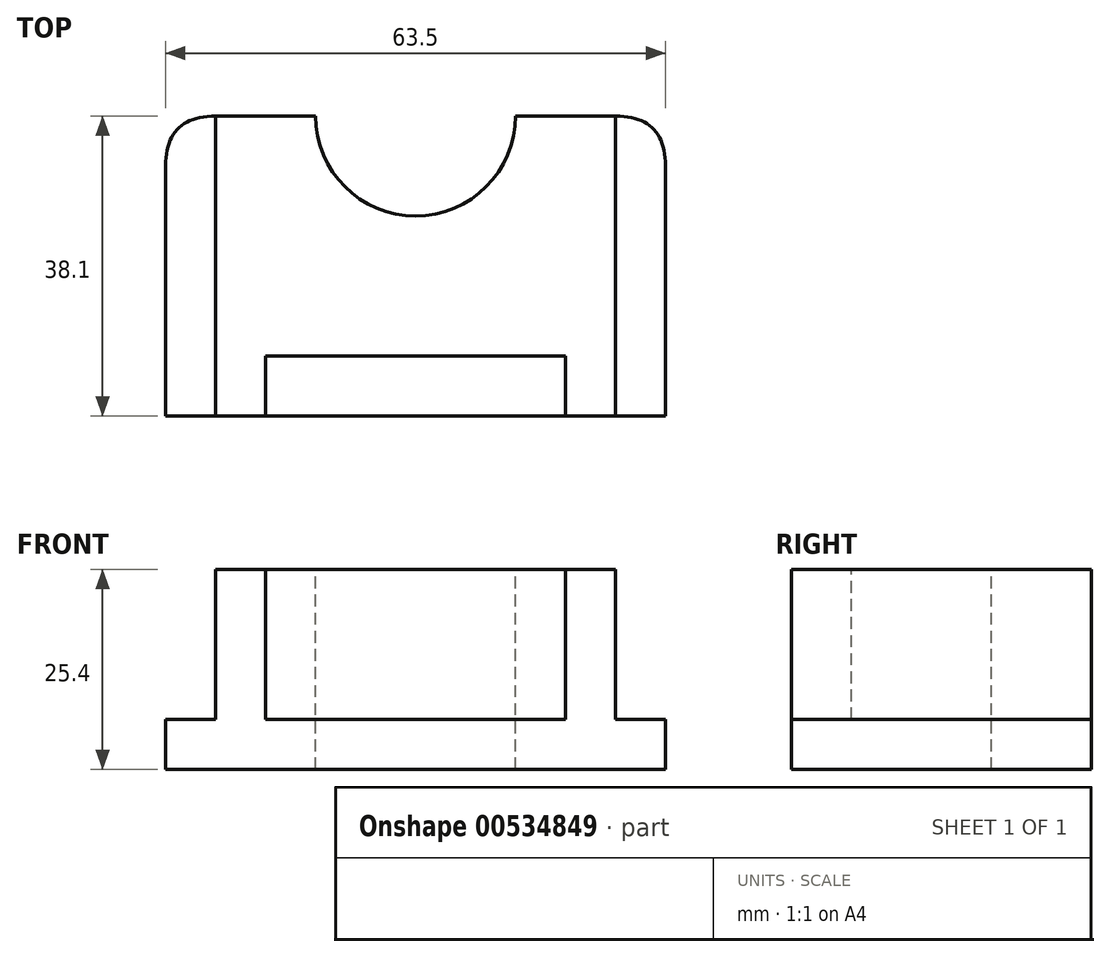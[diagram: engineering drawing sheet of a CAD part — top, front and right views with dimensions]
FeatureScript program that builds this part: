
annotation { "Feature Type Name" : "Feature", "Feature Type Description" : "" }
export const myFeature = defineFeature(function(context is Context, id is Id, definition is map)
    precondition{}
    {
        {
            var Q0;
            Q0=qCreatedBy(makeId("Top.planeOp"),FACE);
            var sketch = newSketch(context, id + "F0", { "sketchPlane" : qUnion([Q0])});
            skLineSegment(sketch, "E0.bottom", {"start": v(31.75, -19.05) * mm, "end": v(-31.75, -19.05) * mm});
            skLineSegment(sketch, "E0.top", {"start": v(31.75, 19.05) * mm, "end": v(-31.75, 19.05) * mm});
            skLineSegment(sketch, "E0.left", {"start": v(31.75, -19.05) * mm, "end": v(31.75, 19.05) * mm});
            skLineSegment(sketch, "E0.right", {"start": v(-31.75, -19.05) * mm, "end": v(-31.75, 19.05) * mm});
            skPoint(sketch, "E0.middle", {"position": v(0, 0) * mm});
            skSolve(sketch);
        }
        {
            var Q0;
            Q0 = qSketchRegion(id + "F0", true);
            extrude(context, id + "F1", {"entities" : qUnion([Q0]), "depth" : 6.35 * mm, "offsetDistance" : 25.4 * mm});
        }
        {
            var Q0;
            Q0=makeQuery(id+"F1.opExtrude","SWEPT_EDGE",EDGE,{"disambiguationData":[OSD([sQuery(id+"F0.wireOp",EDGE,"E0.top"),sQuery(id+"F0.wireOp",EDGE,"E0.right")])]});
            var Q1;
            Q1=makeQuery(id+"F1.opExtrude","SWEPT_EDGE",EDGE,{"disambiguationData":[OSD([sQuery(id+"F0.wireOp",EDGE,"E0.top"),sQuery(id+"F0.wireOp",EDGE,"E0.left")])]});
            fillet(context, id + "F2", {"entities" : qUnion([Q0, Q1]), "radius" : 6.35 * mm, "rho" : 0.5, "crossSection" : FilletCrossSection.CONIC, "allowEdgeOverflow" : false});
        }
        {
            var Q0;
            Q0=makeQuery(id+"F1.opExtrude","CAP_FACE",FACE,{"disambiguationData":[OSD([sQuery(id+"F0.wireOp",EDGE,"E0.bottom"),sQuery(id+"F0.wireOp",EDGE,"E0.top"),sQuery(id+"F0.wireOp",EDGE,"E0.left"),sQuery(id+"F0.wireOp",EDGE,"E0.right")])],"isStart":false});
            var sketch = newSketch(context, id + "F3", { "sketchPlane" : qUnion([Q0])});
            skLineSegment(sketch, "E1.bottom", {"start": v(-25.4, 19.05) * mm, "end": v(25.4, 19.05) * mm});
            skLineSegment(sketch, "E1.top", {"start": v(-25.4, -19.05) * mm, "end": v(25.4, -19.05) * mm});
            skLineSegment(sketch, "E1.left", {"start": v(-25.4, 19.05) * mm, "end": v(-25.4, -19.05) * mm});
            skLineSegment(sketch, "E1.right", {"start": v(25.4, 19.05) * mm, "end": v(25.4, -19.05) * mm});
            skSolve(sketch);
        }
        {
            var Q0;
            Q0 = qSketchRegion(id + "F3", true);
            extrude(context, id + "F4", {"entities" : qUnion([Q0]), "operationType" : NewBodyOperationType.ADD, "depth" : 19.05 * mm, "offsetDistance" : 25.4 * mm});
        }
        {
            var Q0;
            Q0=makeQuery(id+"F4.opExtrude","CAP_FACE",FACE,{"disambiguationData":[OSD([sQuery(id+"F3.wireOp",EDGE,"E1.bottom"),sQuery(id+"F3.wireOp",EDGE,"E1.top"),sQuery(id+"F3.wireOp",EDGE,"E1.left"),sQuery(id+"F3.wireOp",EDGE,"E1.right")])],"isStart":false});
            var sketch = newSketch(context, id + "F5", { "sketchPlane" : qUnion([Q0])});
            skLineSegment(sketch, "E2.bottom", {"start": v(19.05, -19.05) * mm, "end": v(-19.05, -19.05) * mm});
            skLineSegment(sketch, "E2.top", {"start": v(19.05, -11.44) * mm, "end": v(-19.05, -11.44) * mm});
            skLineSegment(sketch, "E2.left", {"start": v(19.05, -19.05) * mm, "end": v(19.05, -11.44) * mm});
            skLineSegment(sketch, "E2.right", {"start": v(-19.05, -19.05) * mm, "end": v(-19.05, -11.44) * mm});
            skPoint(sketch, "E2.middle", {"position": v(0, -15.25) * mm});
            skSolve(sketch);
        }
        {
            var Q0;
            Q0=makeQuery(id+"F5.imprint","IMPRINT",FACE,{"disambiguationData":[TD([[makeQuery(id+"F5.imprint","IMPRINT",EDGE,{"derivedFrom":sQuery(id+"F5.wireOp",EDGE,"E2.bottom")}),-1.0]])]});
            var Q1;
            Q1=sQuery(id+"F5.wireOp",EDGE,"E2.bottom");
            extrude(context, id + "F6", {"entities" : qUnion([Q0]), "operationType" : NewBodyOperationType.REMOVE, "surfaceEntities" : qUnion([Q1]), "oppositeDirection" : true, "depth" : 19.05 * mm, "offsetDistance" : 25.4 * mm});
        }
        {
            var Q0;
            Q0=makeQuery(id+"F4.opExtrude","CAP_FACE",FACE,{"disambiguationData":[OSD([sQuery(id+"F3.wireOp",EDGE,"E1.bottom"),sQuery(id+"F3.wireOp",EDGE,"E1.top"),sQuery(id+"F3.wireOp",EDGE,"E1.left"),sQuery(id+"F3.wireOp",EDGE,"E1.right")])],"isStart":false});
            var sketch = newSketch(context, id + "F7", { "sketchPlane" : qUnion([Q0])});
            skCircle(sketch, "E3", {"center": v(0, 19.05) * mm, "radius": 12.7 * mm});
            skSolve(sketch);
        }
        {
            var Q0;
            Q0 = qSketchRegion(id + "F7", true);
            extrude(context, id + "F8", {"entities" : qUnion([Q0]), "operationType" : NewBodyOperationType.REMOVE, "oppositeDirection" : true, "depth" : 25.4 * mm, "offsetDistance" : 25.4 * mm});
        }
    });
